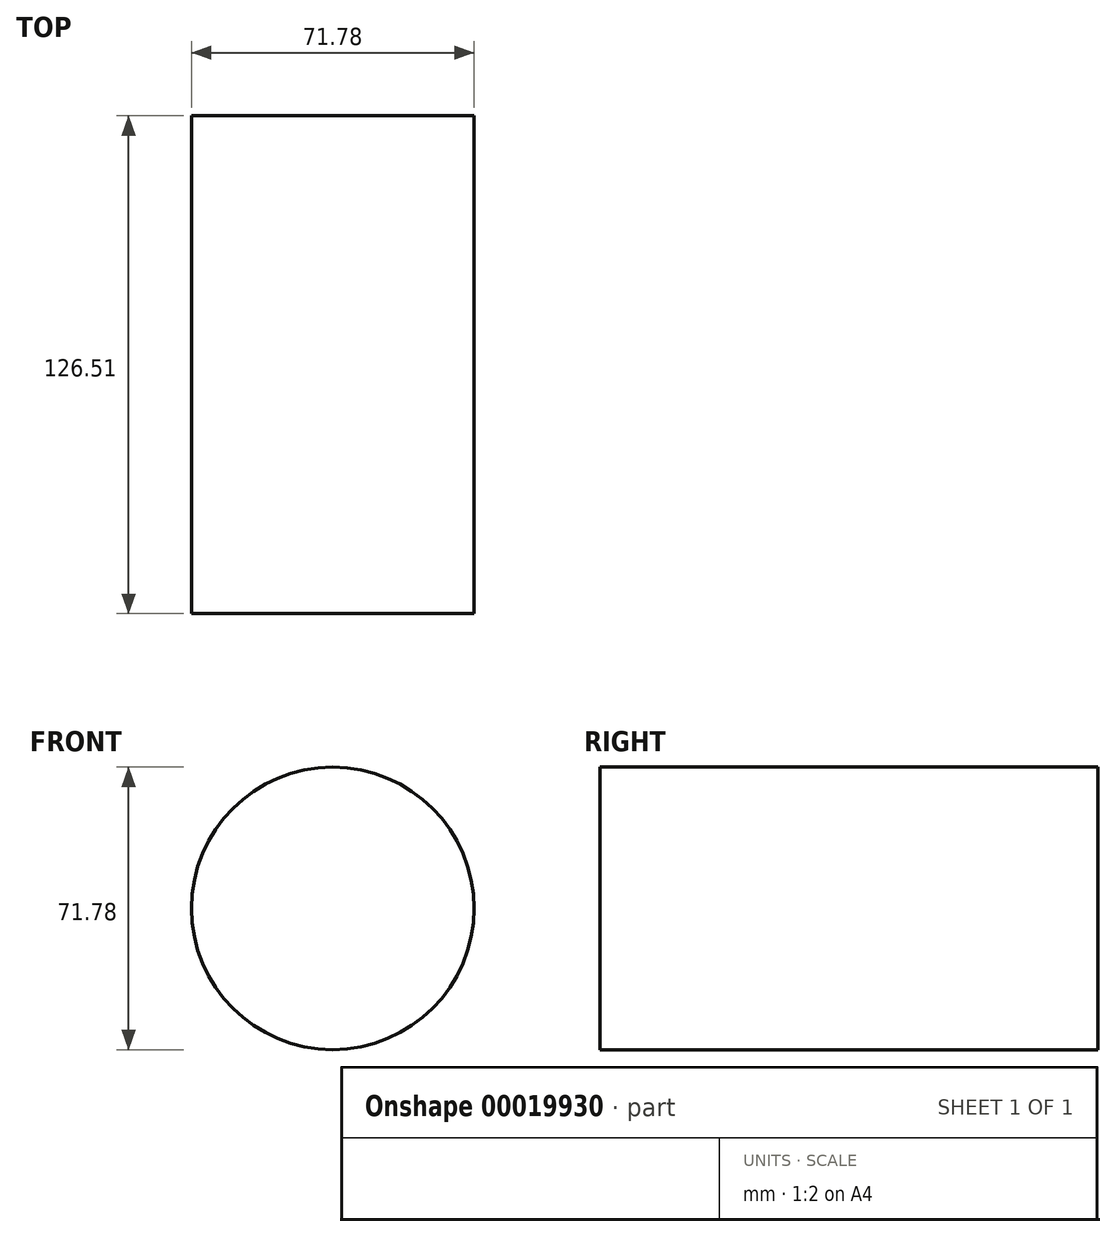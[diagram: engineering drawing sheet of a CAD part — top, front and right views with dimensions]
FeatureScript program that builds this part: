
annotation { "Feature Type Name" : "Feature", "Feature Type Description" : "" }
export const myFeature = defineFeature(function(context is Context, id is Id, definition is map)
    precondition{}
    {
        {
            var Q0;
            Q0=qCreatedBy(makeId("Front.planeOp"),FACE);
            var sketch = newSketch(context, id + "F0", { "sketchPlane" : qUnion([Q0])});
            skCircle(sketch, "E0", {"center": v(0, 0) * mm, "radius": 35.9 * mm});
            skSolve(sketch);
        }
        {
            var Q0;
            Q0 = qSketchRegion(id + "F0", true);
            extrude(context, id + "F1", {"entities" : qUnion([Q0]), "depth" : 25.4 * mm});
        }
        {
            var Q0;
            Q0=makeQuery(id+"F1.opExtrude","CAP_FACE",FACE,{"disambiguationData":[OSD([sQuery(id+"F0.wireOp",EDGE,"E0")])],"isStart":false});
            extrude(context, id + "F2", {"entities" : qUnion([Q0]), "operationType" : NewBodyOperationType.ADD, "depth" : 101.11 * mm});
        }
        {
            var Q0;
            Q0=makeQuery(id+"F2.opExtrude","CAP_FACE",FACE,{"disambiguationData":[OSD([sQuery(id+"F0.wireOp",EDGE,"E0")])],"isStart":false});
            extrude(context, id + "F3", {"entities" : qUnion([Q0]), "operationType" : NewBodyOperationType.ADD, "oppositeDirection" : true, "depth" : 30.06 * mm});
        }
    });
